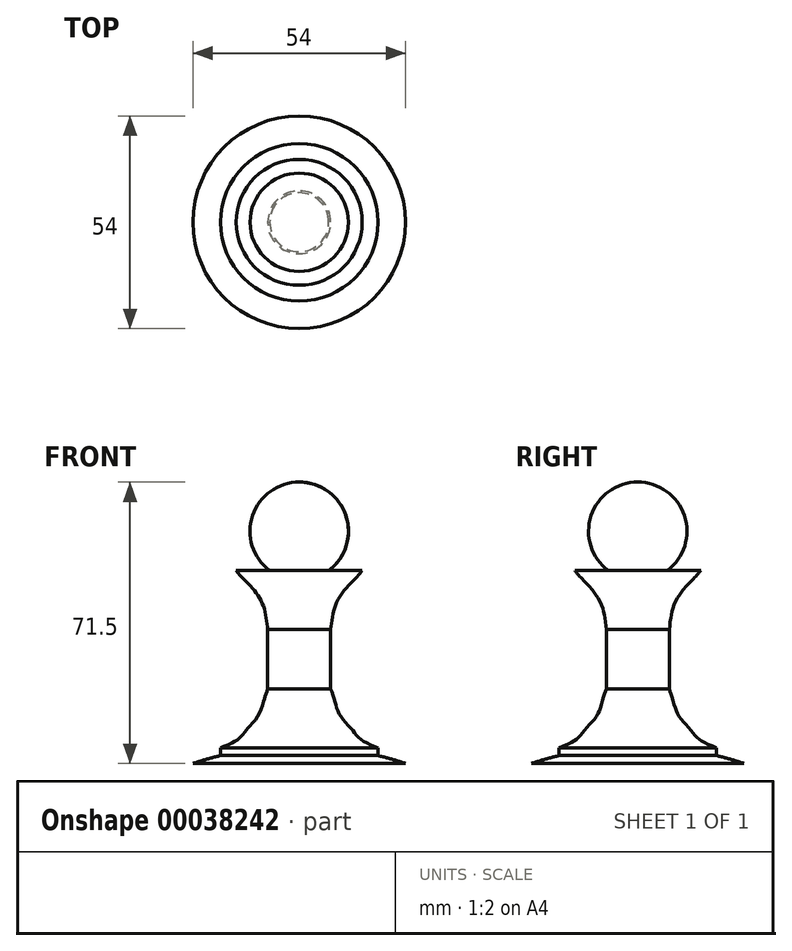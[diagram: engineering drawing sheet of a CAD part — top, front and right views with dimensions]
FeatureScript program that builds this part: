
annotation { "Feature Type Name" : "Feature", "Feature Type Description" : "" }
export const myFeature = defineFeature(function(context is Context, id is Id, definition is map)
    precondition{}
    {
        {
            var Q0;
            Q0=qCreatedBy(makeId("Front.planeOp"),FACE);
            var sketch = newSketch(context, id + "F0", { "sketchPlane" : qUnion([Q0])});
            skArc(sketch, "E0", {"start": v(7.5, 6.9) * mm, "mid": v(11.86, 20.85) * mm, "end": v(0, 29.4) * mm});
            skLineSegment(sketch, "E1", {"start": v(8, -8.1) * mm, "end": v(8, -23.1) * mm});
            skPoint(sketch, "E2.end.orphan", {"position": v(0, -23.1) * mm});
            skLineSegment(sketch, "E3", {"start": v(0, -40.1) * mm, "end": v(0, -42.1) * mm});
            skLineSegment(sketch, "E4", {"start": v(0, -42.1) * mm, "end": v(27, -42.1) * mm});
            skLineSegment(sketch, "E5", {"start": v(7.5, 6.9) * mm, "end": v(16, 6.9) * mm});
            skFitSpline(sketch, "E6", {"points": [v(16, 6.9) * mm, v(15.29, 6.04) * mm, v(13.75, 4.4) * mm, v(11.27, 1.67) * mm, v(9.23, -1.8) * mm, v(8.44, -4.78) * mm, v(8, -8.1) * mm], "startDerivative": vector(-6.15, -7.7) * mm, "endDerivative": vector(-2.16, -18.66) * mm});
            skFitSpline(sketch, "E7", {"points": [v(8, -23.1) * mm, v(9.18, -26.84) * mm, v(10.5, -30.1) * mm, v(13.52, -33.65) * mm, v(15.55, -35.95) * mm, v(20, -38.1) * mm], "startDerivative": vector(6.23, -19.23) * mm, "endDerivative": vector(22.77, -8.9) * mm});
            skLineSegment(sketch, "E8", {"start": v(20, -38.1) * mm, "end": v(20, -40.1) * mm});
            skPoint(sketch, "E9.orphan", {"position": v(24, -40.1) * mm});
            skFitSpline(sketch, "E10", {"points": [v(20, -40.1) * mm, v(23.56, -41.02) * mm, v(27, -42.1) * mm], "startDerivative": vector(7.13, -1.73) * mm, "endDerivative": vector(6.87, -2.27) * mm});
            skLineSegment(sketch, "E11", {"start": v(0, 29.4) * mm, "end": v(0, -42.1) * mm});
            skSolve(sketch);
        }
        {
            var Q0;
            {var subQ0=sQuery(id+"F0.wireOp",EDGE,"E0");Q0=makeQuery(id+"F0.imprint","IMPRINT",FACE,{"disambiguationData":[TD([[makeQuery(id+"F0.imprint","IMPRINT",EDGE,{"derivedFrom":subQ0}),1.0]])]});}
            var Q1;
            Q1=sQuery(id+"F0.wireOp",EDGE,"E11");
            revolve(context, id + "F1", {"entities" : qUnion([Q0]), "axis" : qUnion([Q1]), "revolveType" : RevolveType.FULL});
        }
    });
